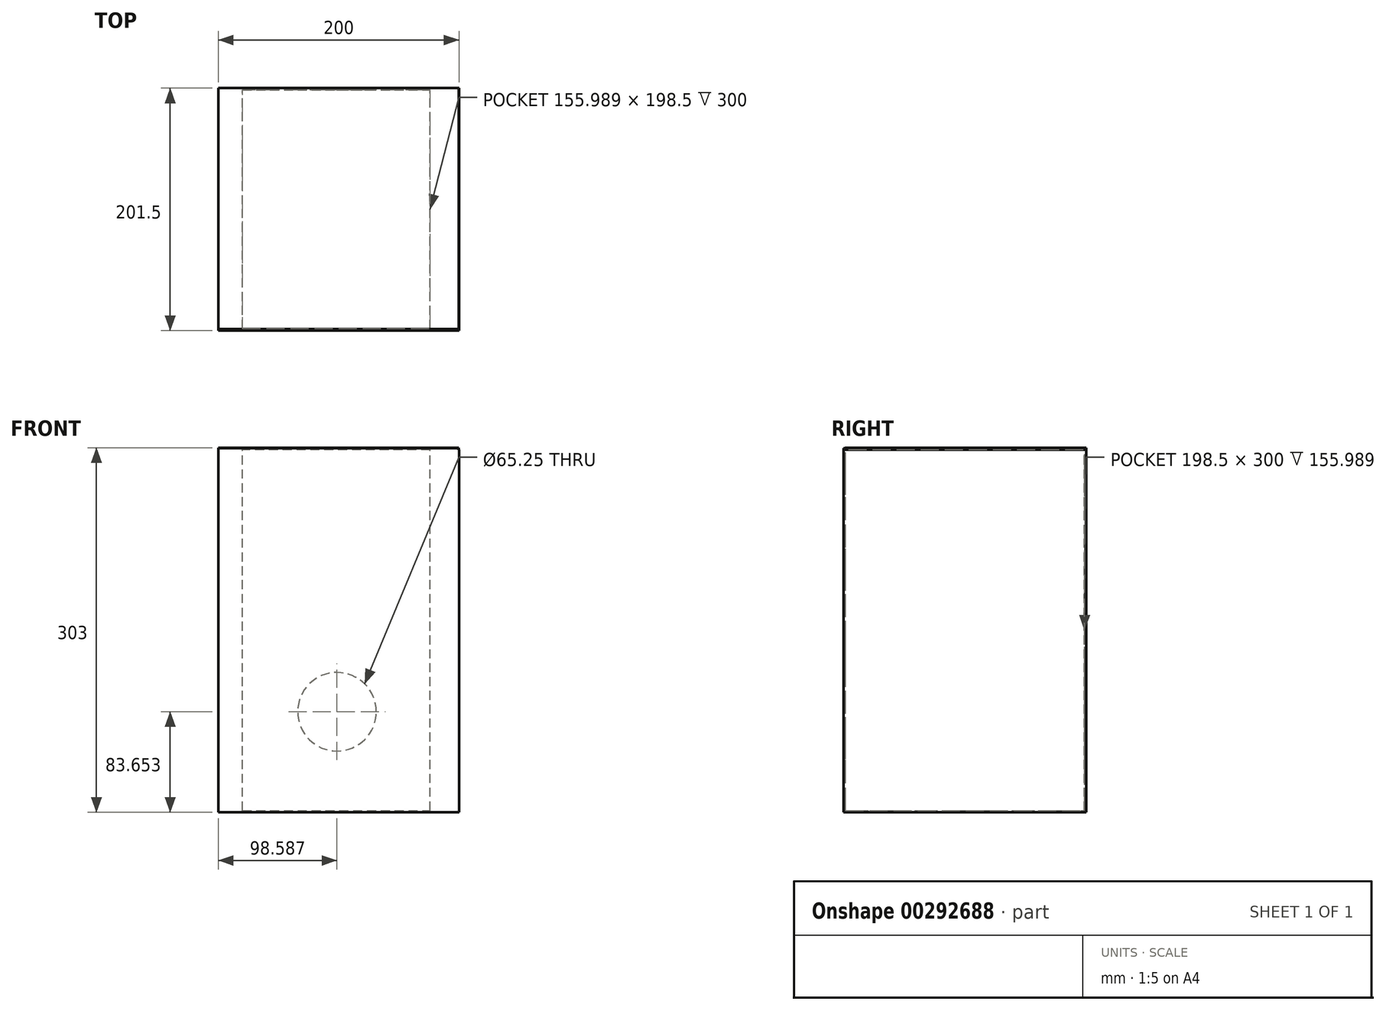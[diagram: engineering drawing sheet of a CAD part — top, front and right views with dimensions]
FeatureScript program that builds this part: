
annotation { "Feature Type Name" : "Feature", "Feature Type Description" : "" }
export const myFeature = defineFeature(function(context is Context, id is Id, definition is map)
    precondition{}
    {
        {
            var Q0;
            Q0=qCreatedBy(makeId("Front.planeOp"),FACE);
            var sketch = newSketch(context, id + "F0", { "sketchPlane" : qUnion([Q0])});
            skLineSegment(sketch, "E0.bottom", {"start": v(0, 0) * mm, "end": v(200, 0) * mm});
            skLineSegment(sketch, "E0.top", {"start": v(0, 300) * mm, "end": v(200, 300) * mm});
            skLineSegment(sketch, "E0.left", {"start": v(0, 0) * mm, "end": v(0, 300) * mm});
            skLineSegment(sketch, "E0.right", {"start": v(200, 0) * mm, "end": v(200, 300) * mm});
            skSolve(sketch);
        }
        {
            var Q0;
            Q0 = qSketchRegion(id + "F0", true);
            extrude(context, id + "F1", {"entities" : qUnion([Q0]), "depth" : 1.5 * mm});
        }
        {
            var Q0;
            Q0=qCreatedBy(makeId("Front.planeOp"),FACE);
            var sketch = newSketch(context, id + "F2", { "sketchPlane" : qUnion([Q0])});
            skLineSegment(sketch, "E1.bottom", {"start": v(0, 0) * mm, "end": v(20, 0) * mm});
            skLineSegment(sketch, "E1.top", {"start": v(0, 300) * mm, "end": v(20, 300) * mm});
            skLineSegment(sketch, "E1.left", {"start": v(0, 0) * mm, "end": v(0, 300) * mm});
            skLineSegment(sketch, "E1.right", {"start": v(20, 0) * mm, "end": v(20, 300) * mm});
            skSolve(sketch);
        }
        {
            var Q0;
            Q0 = qSketchRegion(id + "F2", true);
            extrude(context, id + "F3", {"entities" : qUnion([Q0]), "operationType" : NewBodyOperationType.ADD, "depth" : 200 * mm});
        }
        {
            var Q0;
            Q0=makeQuery(id+"F1.opExtrude","CAP_FACE",FACE,{"disambiguationData":[OSD([sQuery(id+"F0.wireOp",EDGE,"E0.bottom"),sQuery(id+"F0.wireOp",EDGE,"E0.top"),sQuery(id+"F0.wireOp",EDGE,"E0.left"),sQuery(id+"F0.wireOp",EDGE,"E0.right")])],"isStart":false});
            var sketch = newSketch(context, id + "F4", { "sketchPlane" : qUnion([Q0])});
            skLineSegment(sketch, "E2.bottom", {"start": v(200, 0) * mm, "end": v(175.99, 0) * mm});
            skLineSegment(sketch, "E2.top", {"start": v(200, 300) * mm, "end": v(175.99, 300) * mm});
            skLineSegment(sketch, "E2.left", {"start": v(200, 0) * mm, "end": v(200, 300) * mm});
            skLineSegment(sketch, "E2.right", {"start": v(175.99, 0) * mm, "end": v(175.99, 300) * mm});
            skSolve(sketch);
        }
        {
            var Q0;
            Q0 = qSketchRegion(id + "F4", true);
            extrude(context, id + "F5", {"entities" : qUnion([Q0]), "operationType" : NewBodyOperationType.ADD, "depth" : 200 * mm});
        }
        {
            var Q0;
            Q0=makeQuery(id+"F3.opExtrude","CAP_FACE",FACE,{"disambiguationData":[OSD([sQuery(id+"F2.wireOp",EDGE,"E1.bottom"),sQuery(id+"F2.wireOp",EDGE,"E1.top"),sQuery(id+"F2.wireOp",EDGE,"E1.left"),sQuery(id+"F2.wireOp",EDGE,"E1.right")])],"isStart":false});
            var sketch = newSketch(context, id + "F6", { "sketchPlane" : qUnion([Q0])});
            skLineSegment(sketch, "E3.bottom", {"start": v(0, 0) * mm, "end": v(199.52, 0) * mm});
            skLineSegment(sketch, "E3.top", {"start": v(0, 301.07) * mm, "end": v(199.52, 301.07) * mm});
            skLineSegment(sketch, "E3.left", {"start": v(0, 0) * mm, "end": v(0, 301.07) * mm});
            skLineSegment(sketch, "E3.right", {"start": v(199.52, 0) * mm, "end": v(199.52, 301.07) * mm});
            skSolve(sketch);
        }
        {
            var Q0;
            Q0 = qSketchRegion(id + "F6", true);
            extrude(context, id + "F7", {"entities" : qUnion([Q0]), "operationType" : NewBodyOperationType.ADD, "depth" : 1.5 * mm});
        }
        {
            var Q0;
            Q0=makeQuery(id+"F5.boolean.opBoolean","MERGE",FACE,{"derivedFrom":[makeQuery(id+"F3.boolean.opBoolean","MERGE",FACE,{"derivedFrom":[makeQuery(id+"F1.opExtrude","SWEPT_FACE",FACE,{"disambiguationData":[OSD([sQuery(id+"F0.wireOp",EDGE,"E0.top")])]}),makeQuery(id+"F3.opExtrude","SWEPT_FACE",FACE,{"disambiguationData":[OSD([sQuery(id+"F2.wireOp",EDGE,"E1.top")])]})]}),makeQuery(id+"F5.opExtrude","SWEPT_FACE",FACE,{"disambiguationData":[OSD([sQuery(id+"F4.wireOp",EDGE,"E2.top")])]})]});
            var sketch = newSketch(context, id + "F8", { "sketchPlane" : qUnion([Q0])});
            skLineSegment(sketch, "E4.bottom", {"start": v(20, -1.5) * mm, "end": v(175.99, -1.5) * mm});
            skLineSegment(sketch, "E4.top", {"start": v(20, -200) * mm, "end": v(175.99, -200) * mm});
            skLineSegment(sketch, "E4.left", {"start": v(20, -1.5) * mm, "end": v(20, -200) * mm});
            skLineSegment(sketch, "E4.right", {"start": v(175.99, -1.5) * mm, "end": v(175.99, -200) * mm});
            skSolve(sketch);
        }
        {
            var Q0;
            Q0=makeQuery(id+"F1.opExtrude","CAP_FACE",FACE,{"disambiguationData":[OSD([sQuery(id+"F0.wireOp",EDGE,"E0.bottom"),sQuery(id+"F0.wireOp",EDGE,"E0.top"),sQuery(id+"F0.wireOp",EDGE,"E0.left"),sQuery(id+"F0.wireOp",EDGE,"E0.right")])],"isStart":true});
            var sketch = newSketch(context, id + "F9", { "sketchPlane" : qUnion([Q0])});
            skCircle(sketch, "E5", {"center": v(-98.59, 82.15) * mm, "radius": 32.62 * mm});
            skSolve(sketch);
        }
        {
            var Q0;
            Q0 = qSketchRegion(id + "F9", true);
            extrude(context, id + "F10", {"entities" : qUnion([Q0]), "operationType" : NewBodyOperationType.REMOVE, "oppositeDirection" : true, "depth" : 1.5 * mm});
        }
        {
            var Q0;
            Q0=makeQuery(id+"F7.boolean.opBoolean","MERGE",FACE,{"derivedFrom":[makeQuery(id+"F5.boolean.opBoolean","MERGE",FACE,{"derivedFrom":[makeQuery(id+"F3.boolean.opBoolean","MERGE",FACE,{"derivedFrom":[makeQuery(id+"F1.opExtrude","SWEPT_FACE",FACE,{"disambiguationData":[OSD([sQuery(id+"F0.wireOp",EDGE,"E0.bottom")])]}),makeQuery(id+"F3.opExtrude","SWEPT_FACE",FACE,{"disambiguationData":[OSD([sQuery(id+"F2.wireOp",EDGE,"E1.bottom")])]})]}),makeQuery(id+"F5.opExtrude","SWEPT_FACE",FACE,{"disambiguationData":[OSD([sQuery(id+"F4.wireOp",EDGE,"E2.bottom")])]})]}),makeQuery(id+"F7.opExtrude","SWEPT_FACE",FACE,{"disambiguationData":[OSD([sQuery(id+"F6.wireOp",EDGE,"E3.bottom")])]})]});
            var sketch = newSketch(context, id + "F11", { "sketchPlane" : qUnion([Q0])});
            skLineSegment(sketch, "E6.bottom", {"start": v(0, 201.5) * mm, "end": v(200, 201.5) * mm});
            skLineSegment(sketch, "E6.top", {"start": v(0, 0) * mm, "end": v(200, 0) * mm});
            skLineSegment(sketch, "E6.left", {"start": v(0, 201.5) * mm, "end": v(0, 0) * mm});
            skLineSegment(sketch, "E6.right", {"start": v(200, 201.5) * mm, "end": v(200, 0) * mm});
            skSolve(sketch);
        }
        {
            var Q0;
            Q0 = qSketchRegion(id + "F11", true);
            extrude(context, id + "F12", {"entities" : qUnion([Q0]), "operationType" : NewBodyOperationType.ADD, "depth" : 1.5 * mm});
        }
        {
            var Q0;
            Q0=makeQuery(id+"F8.imprint","IMPRINT",FACE,{"disambiguationData":[TD([[makeQuery(id+"F8.imprint","IMPRINT",EDGE,{"derivedFrom":sQuery(id+"F8.wireOp",EDGE,"E4.bottom")}),1.0]])]});
            var sketch = newSketch(context, id + "F13", { "sketchPlane" : qUnion([Q0])});
            skLineSegment(sketch, "E7.bottom", {"start": v(0, 0) * mm, "end": v(199.75, 0) * mm});
            skLineSegment(sketch, "E7.top", {"start": v(0, -200.25) * mm, "end": v(199.75, -200.25) * mm});
            skLineSegment(sketch, "E7.left", {"start": v(0, 0) * mm, "end": v(0, -200.25) * mm});
            skLineSegment(sketch, "E7.right", {"start": v(199.75, 0) * mm, "end": v(199.75, -200.25) * mm});
            skSolve(sketch);
        }
        {
            var Q0;
            Q0 = qSketchRegion(id + "F13", true);
            extrude(context, id + "F14", {"entities" : qUnion([Q0]), "operationType" : NewBodyOperationType.ADD, "depth" : 1.5 * mm});
        }
    });
